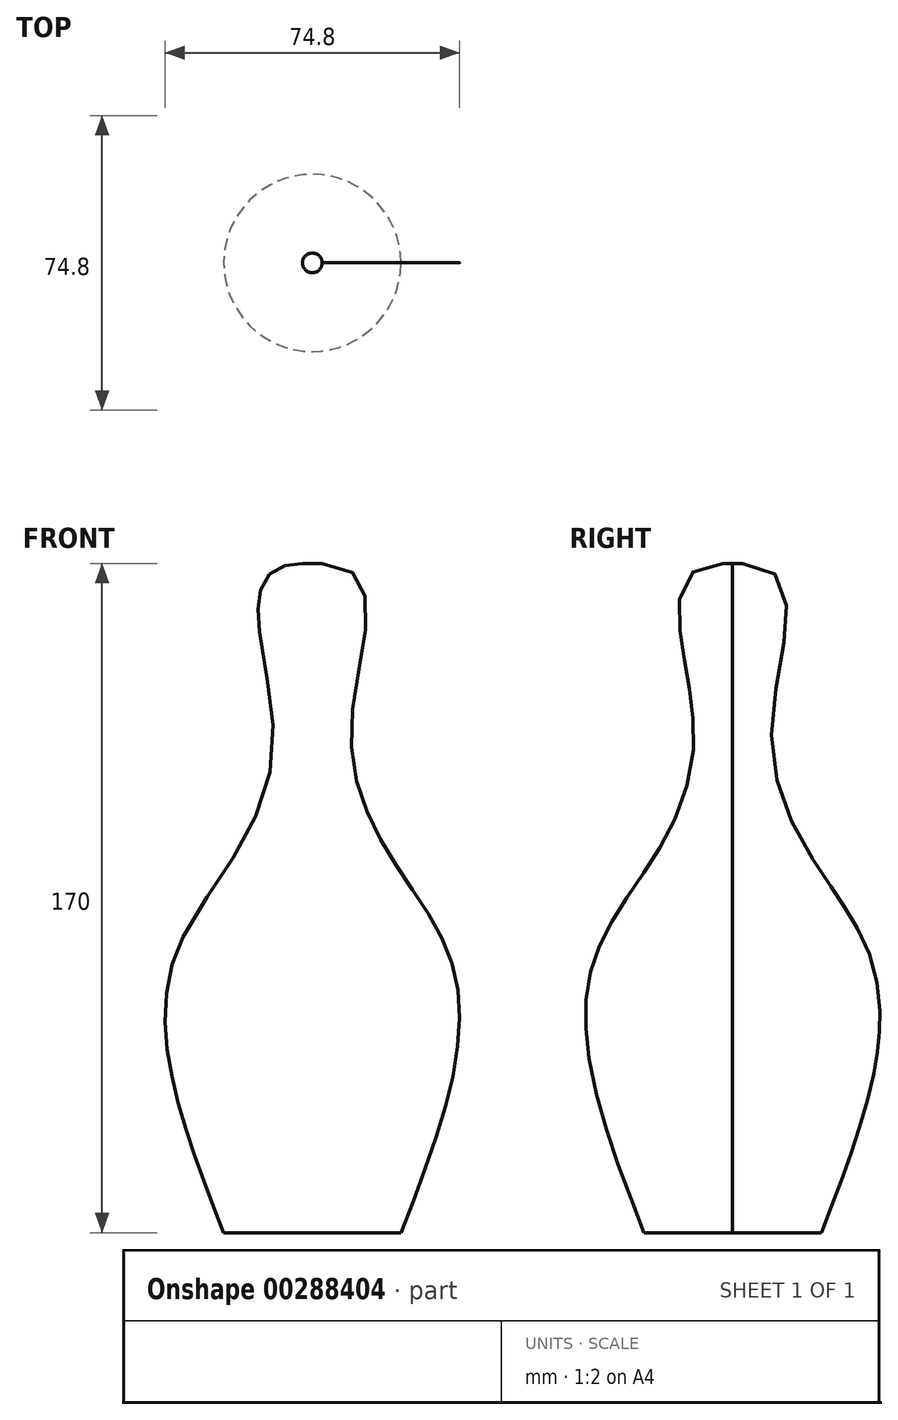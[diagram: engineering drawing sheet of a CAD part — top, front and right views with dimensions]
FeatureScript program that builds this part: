
annotation { "Feature Type Name" : "Feature", "Feature Type Description" : "" }
export const myFeature = defineFeature(function(context is Context, id is Id, definition is map)
    precondition{}
    {
        {
            var Q0;
            Q0=qCreatedBy(makeId("Top.planeOp"),FACE);
            cPlane(context, id + "F0", {"entities" : qUnion([Q0]), "cplaneType" : CPlaneType.OFFSET, "offset" : 70 * mm, "width" : 150 * mm, "height" : 150 * mm});
        }
        {
            var Q0;
            Q0=qCreatedBy(makeId("Top.planeOp"),FACE);
            cPlane(context, id + "F1", {"entities" : qUnion([Q0]), "cplaneType" : CPlaneType.OFFSET, "offset" : 130 * mm, "width" : 150 * mm, "height" : 150 * mm});
        }
        {
            var Q0;
            Q0=qCreatedBy(id+"F1.planeOp",FACE);
            cPlane(context, id + "F2", {"entities" : qUnion([Q0]), "cplaneType" : CPlaneType.OFFSET, "offset" : 40 * mm, "width" : 150 * mm, "height" : 150 * mm});
        }
        {
            var Q0;
            Q0=qCreatedBy(makeId("Top.planeOp"),FACE);
            var sketch = newSketch(context, id + "F3", { "sketchPlane" : qUnion([Q0])});
            skCircle(sketch, "E0", {"center": v(0, 0) * mm, "radius": 22.5 * mm});
            skSolve(sketch);
        }
        {
            var Q0;
            Q0=qCreatedBy(id+"F0.planeOp",FACE);
            var sketch = newSketch(context, id + "F4", { "sketchPlane" : qUnion([Q0])});
            skCircle(sketch, "E1", {"center": v(0, 0) * mm, "radius": 35 * mm});
            skSolve(sketch);
        }
        {
            var Q0;
            Q0=qCreatedBy(id+"F1.planeOp",FACE);
            var sketch = newSketch(context, id + "F5", { "sketchPlane" : qUnion([Q0])});
            skCircle(sketch, "E2", {"center": v(0, 0) * mm, "radius": 10 * mm});
            skSolve(sketch);
        }
        {
            var Q0;
            Q0=qCreatedBy(id+"F2.planeOp",FACE);
            var sketch = newSketch(context, id + "F6", { "sketchPlane" : qUnion([Q0])});
            skCircle(sketch, "E3", {"center": v(0, 0) * mm, "radius": 2.5 * mm});
            skSolve(sketch);
        }
        {
            var Q0;
            Q0=makeQuery(id+"F3.imprint","IMPRINT",FACE,{"disambiguationData":[TD([[makeQuery(id+"F3.imprint","IMPRINT",EDGE,{"derivedFrom":sQuery(id+"F3.wireOp",EDGE,"E0")}),1.0]])]});
            var Q1;
            Q1=makeQuery(id+"F4.imprint","IMPRINT",FACE,{"disambiguationData":[TD([[makeQuery(id+"F4.imprint","IMPRINT",EDGE,{"derivedFrom":sQuery(id+"F4.wireOp",EDGE,"E1")}),1.0]])]});
            var Q2;
            Q2=makeQuery(id+"F5.imprint","IMPRINT",FACE,{"disambiguationData":[TD([[makeQuery(id+"F5.imprint","IMPRINT",EDGE,{"derivedFrom":sQuery(id+"F5.wireOp",EDGE,"E2")}),1.0]])]});
            var Q3;
            Q3=makeQuery(id+"F6.imprint","IMPRINT",FACE,{"disambiguationData":[TD([[makeQuery(id+"F6.imprint","IMPRINT",EDGE,{"derivedFrom":sQuery(id+"F6.wireOp",EDGE,"E3")}),1.0]])]});
            loft(context, id + "F7", {"endCondition" : LoftEndDerivativeType.TANGENT_TO_PROFILE, "endMagnitude" : 12, "sheetProfilesArray" : [{ "sheetProfileEntities" : qUnion([Q0]) }, { "sheetProfileEntities" : qUnion([Q1]) }, { "sheetProfileEntities" : qUnion([Q2]) }, { "sheetProfileEntities" : qUnion([Q3]) }]});
        }
    });
